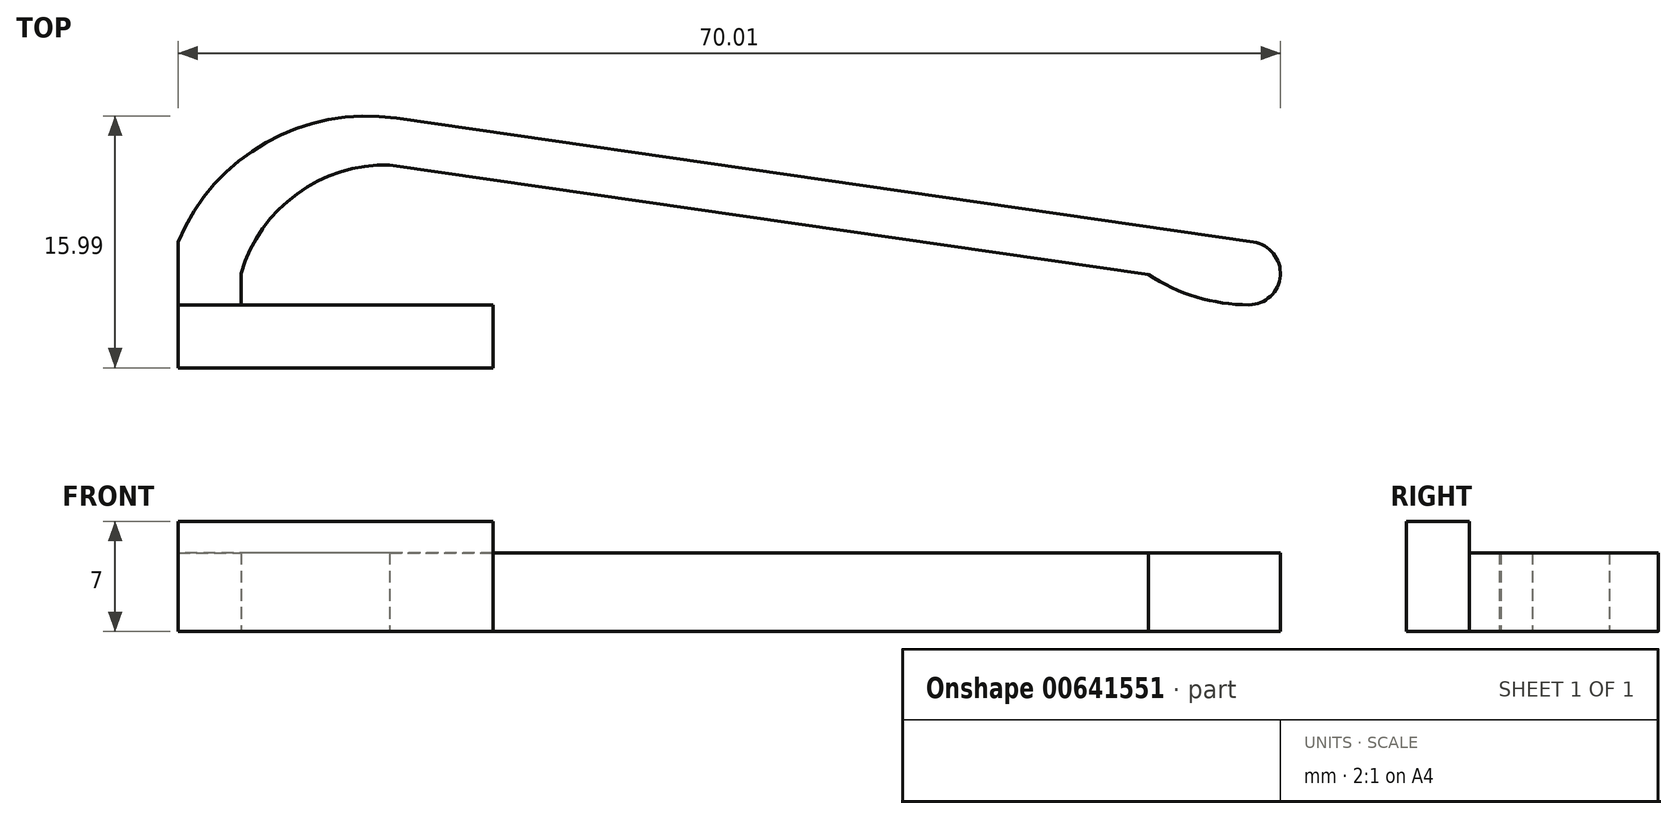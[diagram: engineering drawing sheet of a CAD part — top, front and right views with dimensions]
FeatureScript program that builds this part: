
annotation { "Feature Type Name" : "Feature", "Feature Type Description" : "" }
export const myFeature = defineFeature(function(context is Context, id is Id, definition is map)
    precondition{}
    {
        {
            var Q0;
            Q0=qCreatedBy(makeId("Top.planeOp"),FACE);
            var sketch = newSketch(context, id + "F0", { "sketchPlane" : qUnion([Q0])});
            skLineSegment(sketch, "E0.right", {"start": v(70, 0) * mm, "end": v(70, 4) * mm, "construction": true});
            skLineSegment(sketch, "E1", {"start": v(70, 4) * mm, "end": v(68, 4) * mm, "construction": true});
            skLineSegment(sketch, "E2", {"start": v(68, 4) * mm, "end": v(68, 6) * mm, "construction": true});
            skArc(sketch, "E3", {"start": v(68, 4) * mm, "mid": v(70, 5.86) * mm, "end": v(68.3, 7.98) * mm});
            skLineSegment(sketch, "E4", {"start": v(68.3, 7.98) * mm, "end": v(13.86, 15.86) * mm});
            skCircle(sketch, "E5", {"center": v(0, 0) * mm, "radius": 3 * mm, "construction": true});
            skLineSegment(sketch, "E6.trimOffspring", {"start": v(20, 4) * mm, "end": v(70, 4) * mm, "construction": true});
            skLineSegment(sketch, "E7", {"start": v(62.06, 8.88) * mm, "end": v(61.63, 5.91) * mm, "construction": true});
            skArc(sketch, "E8", {"start": v(61.63, 5.91) * mm, "mid": v(64.68, 4.49) * mm, "end": v(68, 4) * mm});
            skLineSegment(sketch, "E9", {"start": v(13.86, 15.86) * mm, "end": v(13.43, 12.89) * mm, "construction": true});
            skLineSegment(sketch, "E10", {"start": v(13.43, 12.89) * mm, "end": v(61.63, 5.91) * mm});
            skLineSegment(sketch, "E11", {"start": v(0, 0) * mm, "end": v(20, 0) * mm});
            skLineSegment(sketch, "E12", {"start": v(20, 0) * mm, "end": v(70, 0) * mm, "construction": true});
            skLineSegment(sketch, "E13", {"start": v(0, 0) * mm, "end": v(0, 16.96) * mm, "construction": true});
            skLineSegment(sketch, "E14", {"start": v(0, 0) * mm, "end": v(0, 8) * mm});
            skArc(sketch, "E15", {"start": v(13.86, 15.86) * mm, "mid": v(5.59, 14.3) * mm, "end": v(0, 8) * mm});
            skLineSegment(sketch, "E16.top", {"start": v(0, 4) * mm, "end": v(20, 4) * mm});
            skLineSegment(sketch, "E16.left", {"start": v(0, 0) * mm, "end": v(0, 4) * mm});
            skLineSegment(sketch, "E17", {"start": v(20, 4) * mm, "end": v(20, 0) * mm});
            skLineSegment(sketch, "E18", {"start": v(0, 4) * mm, "end": v(4, 4) * mm, "construction": true});
            skLineSegment(sketch, "E19", {"start": v(4, 4) * mm, "end": v(4, 6) * mm});
            skArc(sketch, "E20", {"start": v(13.43, 12.89) * mm, "mid": v(7.55, 11.04) * mm, "end": v(4, 6) * mm});
            skSolve(sketch);
        }
        {
            var Q0;
            Q0=makeQuery(id+"F0.imprint","IMPRINT",FACE,{"disambiguationData":[TD([[makeQuery(id+"F0.imprint","IMPRINT",EDGE,{"derivedFrom":sQuery(id+"F0.wireOp",EDGE,"E3")}),1.0]])]});
            extrude(context, id + "F1", {"entities" : qUnion([Q0]), "depth" : 5 * mm, "offsetDistance" : 25 * mm});
        }
        {
            var Q0;
            {var subQ4=sQuery(id+"F0.wireOp",EDGE,"E11");Q0=makeQuery(id+"F0.imprint","IMPRINT",FACE,{"disambiguationData":[TD([[makeQuery(id+"F0.imprint","IMPRINT",EDGE,{"derivedFrom":subQ4}),1.0]])]});}
            extrude(context, id + "F2", {"entities" : qUnion([Q0]), "operationType" : NewBodyOperationType.ADD, "depth" : 7 * mm, "offsetDistance" : 25 * mm});
        }
    });
